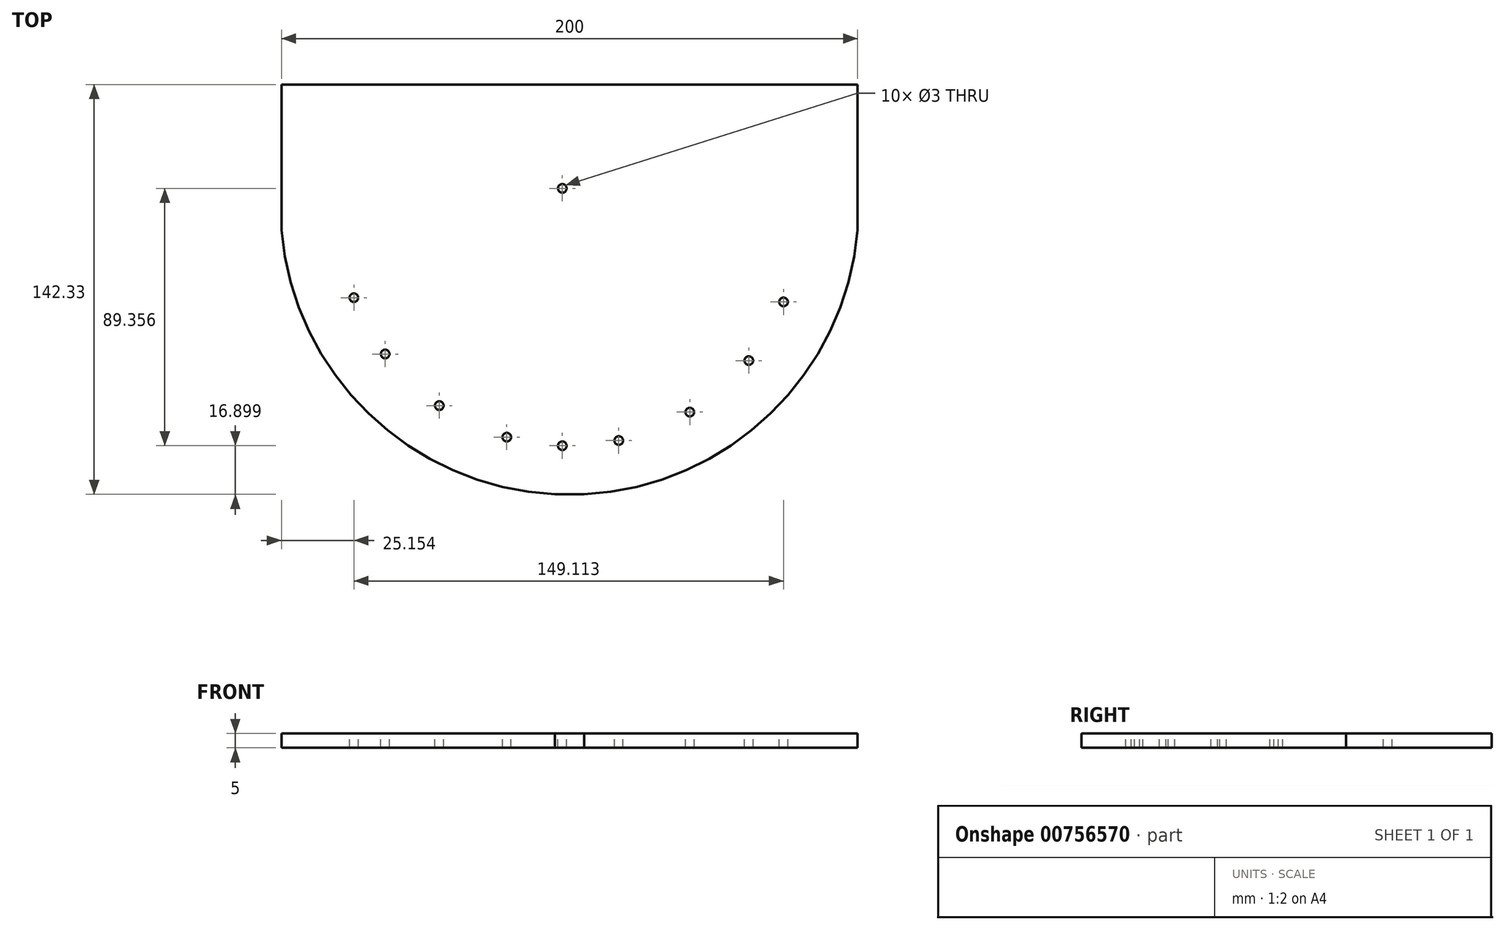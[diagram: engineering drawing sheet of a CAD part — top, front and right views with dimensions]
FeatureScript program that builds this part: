
annotation { "Feature Type Name" : "Feature", "Feature Type Description" : "" }
export const myFeature = defineFeature(function(context is Context, id is Id, definition is map)
    precondition{}
    {
        {
            var Q0;
            Q0=qCreatedBy(makeId("Top.planeOp"),FACE);
            var sketch = newSketch(context, id + "F0", { "sketchPlane" : qUnion([Q0])});
            skLineSegment(sketch, "E0.top", {"start": v(-2.54, -91.79) * mm, "end": v(7.58, -91.79) * mm});
            skLineSegment(sketch, "E0.left", {"start": v(-97.48, 50.54) * mm, "end": v(-97.48, -6.79) * mm});
            skLineSegment(sketch, "E0.right", {"start": v(102.52, 50.54) * mm, "end": v(102.52, 0) * mm});
            skArc(sketch, "E1", {"start": v(-97.48, 0) * mm, "mid": v(2.52, -91.92) * mm, "end": v(102.52, 0) * mm});
            skPoint(sketch, "E1.startSnap0", {"position": v(-97.48, -6.79) * mm});
            skPoint(sketch, "E2.orphan", {"position": v(-97.48, -91.79) * mm});
            skLineSegment(sketch, "E3", {"start": v(-97.48, 50.54) * mm, "end": v(102.52, 50.54) * mm});
            skPoint(sketch, "E3.endSnap0", {"position": v(102.52, 39.1) * mm});
            skPoint(sketch, "E4.orphan", {"position": v(-97.48, 78.21) * mm});
            skPoint(sketch, "E5.orphan", {"position": v(102.52, 78.21) * mm});
            skSolve(sketch);
        }
        {
            var Q0;
            Q0=makeQuery(id+"F0.imprint","IMPRINT",FACE,{"disambiguationData":[TD([[makeQuery(id+"F0.imprint","IMPRINT",EDGE,{"derivedFrom":sQuery(id+"F0.wireOp",EDGE,"E0.bottom")}),-1.0]])]});
            var Q1;
            {var subQ1=sQuery(id+"F0.wireOp",EDGE,"E0.top");Q1=makeQuery(id+"F0.imprint","IMPRINT",FACE,{"disambiguationData":[TD([[makeQuery(id+"F0.imprint","IMPRINT",EDGE,{"derivedFrom":subQ1}),1.0]])]});}
            extrude(context, id + "F1", {"entities" : qUnion([Q0, Q1]), "depth" : 5 * mm, "offsetDistance" : 25 * mm});
        }
        {
            var Q0;
            Q0=makeQuery(id+"F1.opExtrude","CAP_FACE",FACE,{"disambiguationData":[OSD([sQuery(id+"F0.wireOp",EDGE,"E0.bottom"),sQuery(id+"F0.wireOp",EDGE,"E0.top"),sQuery(id+"F0.wireOp",EDGE,"E0.left"),sQuery(id+"F0.wireOp",EDGE,"E0.right"),sQuery(id+"F0.wireOp",EDGE,"E1")])],"isStart":false});
            var sketch = newSketch(context, id + "F2", { "sketchPlane" : qUnion([Q0])});
            skLineSegment(sketch, "E6", {"start": v(-97.48, 0) * mm, "end": v(-77.48, 0) * mm, "construction": true});
            skLineSegment(sketch, "E7", {"start": v(102.52, 0) * mm, "end": v(82.52, 0) * mm, "construction": true});
            skArc(sketch, "E8", {"start": v(-77.48, 0) * mm, "mid": v(2.52, -74.93) * mm, "end": v(82.52, 0) * mm, "construction": true});
            skCircle(sketch, "E9", {"center": v(-72.33, -23.5) * mm, "radius": 1.5 * mm});
            skCircle(sketch, "E10", {"center": v(-61.48, -43.05) * mm, "radius": 1.5 * mm});
            skCircle(sketch, "E11", {"center": v(-42.7, -60.97) * mm, "radius": 1.5 * mm});
            skCircle(sketch, "E12", {"center": v(-19.27, -71.91) * mm, "radius": 1.5 * mm});
            skCircle(sketch, "E13", {"center": v(0, -74.9) * mm, "radius": 1.5 * mm});
            skCircle(sketch, "E14", {"center": v(19.59, -73.1) * mm, "radius": 1.5 * mm});
            skCircle(sketch, "E15", {"center": v(44.26, -63.2) * mm, "radius": 1.5 * mm});
            skCircle(sketch, "E16", {"center": v(64.73, -45.33) * mm, "radius": 1.5 * mm});
            skCircle(sketch, "E17", {"center": v(76.79, -24.95) * mm, "radius": 1.5 * mm});
            skLineSegment(sketch, "E18", {"start": v(-77.48, 0) * mm, "end": v(82.52, 0) * mm, "construction": true});
            skLineSegment(sketch, "E19", {"start": v(0, 45.87) * mm, "end": v(0, -41.66) * mm, "construction": true});
            skLineSegment(sketch, "E20", {"start": v(0, 0) * mm, "end": v(-72.33, -23.5) * mm, "construction": true});
            skLineSegment(sketch, "E21", {"start": v(-61.48, -43.05) * mm, "end": v(0, 0) * mm, "construction": true});
            skLineSegment(sketch, "E22", {"start": v(-42.7, -60.97) * mm, "end": v(0, 0) * mm, "construction": true});
            skLineSegment(sketch, "E23", {"start": v(-19.27, -71.91) * mm, "end": v(0, 0) * mm, "construction": true});
            skLineSegment(sketch, "E24", {"start": v(0, -74.9) * mm, "end": v(0, 0) * mm, "construction": true});
            skLineSegment(sketch, "E25", {"start": v(19.59, -73.1) * mm, "end": v(0, 0) * mm, "construction": true});
            skLineSegment(sketch, "E26", {"start": v(44.26, -63.2) * mm, "end": v(0, 0) * mm, "construction": true});
            skLineSegment(sketch, "E27", {"start": v(64.73, -45.33) * mm, "end": v(0, 0) * mm, "construction": true});
            skLineSegment(sketch, "E28", {"start": v(76.79, -24.95) * mm, "end": v(0, 0) * mm, "construction": true});
            skCircle(sketch, "E29", {"center": v(0, 14.46) * mm, "radius": 1.5 * mm});
            skSolve(sketch);
        }
        {
            var Q0;
            Q0 = qSketchRegion(id + "F2", true);
            extrude(context, id + "F3", {"entities" : qUnion([Q0]), "operationType" : NewBodyOperationType.REMOVE, "oppositeDirection" : true, "depth" : 25 * mm, "offsetDistance" : 25 * mm});
        }
    });
